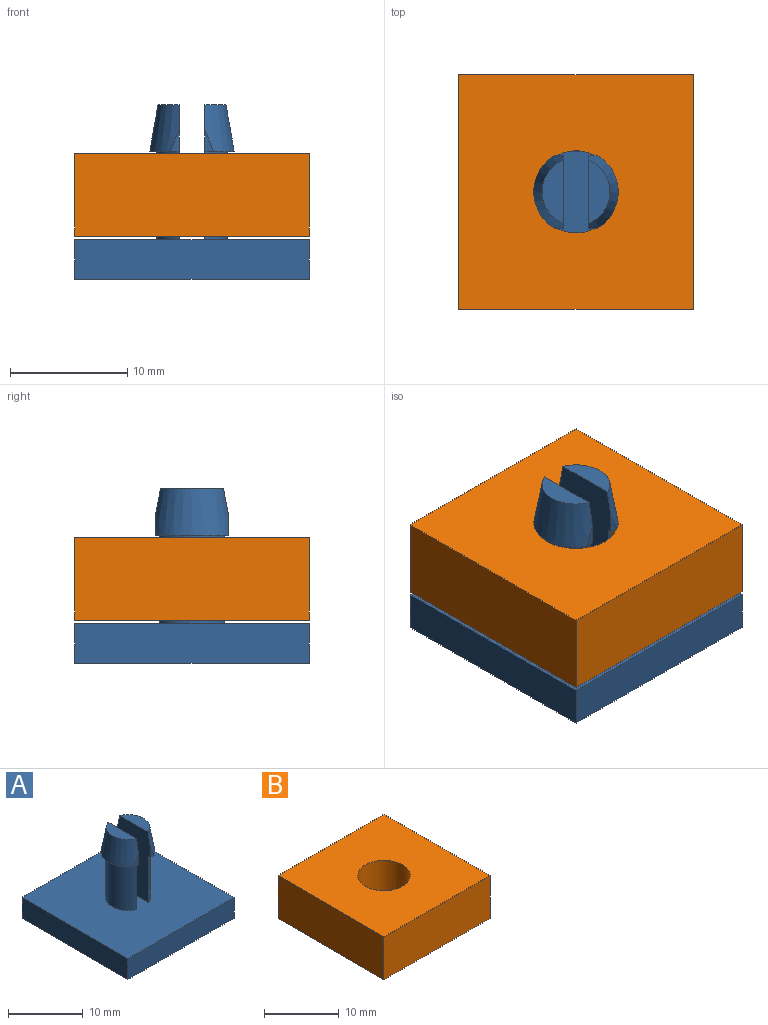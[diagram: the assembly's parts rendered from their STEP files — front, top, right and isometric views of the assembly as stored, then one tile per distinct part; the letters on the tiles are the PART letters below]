
ASSEMBLY  parts=2 mates=1
PART A: 20 faces, bbox 20.1x20.1x15 mm
  f0: plane 6.2x2.5mm, normal (0,0,-1), area 4.6mm2, adj f2,f12,f13,f16,f17
  f1: cone r=3.6mm half-angle=10deg, axis (0,0,-1), area 30.9mm2, adj f3,f11,f14,f18,f19
  f2: cone r=3.6mm half-angle=10deg, axis (0,0,-1), area 30.9mm2, adj f0,f13,f15,f16,f17
  f3: plane 5.36x1.79mm, normal (0,0,1), area 7mm2, adj f1,f11
  f4: plane 20x3.4mm, normal (0,-1,0), area 68mm2, adj f5,f7,f8,f9
  f5: plane 20x3.4mm, normal (1,0,0), area 68mm2, adj f4,f6,f8,f9
  f6: plane 20x3.4mm, normal (0,1,0), area 68mm2, adj f5,f7,f8,f9
  f7: plane 20x3.4mm, normal (-1,0,0), area 68mm2, adj f4,f6,f8,f9
  f8: plane 20x20mm, normal (0,0,1), area 384.6mm2, adj f4,f5,f6,f7,f10,f11,f12,f13
  f9: plane 20x20mm, normal (0,0,-1), area 400mm2, adj f4,f5,f6,f7
  f10: cylinder r=3mm len=7.5mm, axis (0,0,-1), area 53.8mm2, adj f8,f11,f14
  f11: plane 11.51x6.21mm, normal (1,0,0), area 65.7mm2, adj f1,f3,f8,f10,f14,f18,f19
  f12: cylinder r=3mm len=7.5mm, axis (0,0,-1), area 53.8mm2, adj f0,f8,f13
  f13: plane 11.51x6.21mm, normal (-1,0,0), area 65.7mm2, adj f0,f2,f8,f12,f15,f16,f17
  f14: plane 6.2x2.5mm, normal (0,0,-1), area 4.6mm2, adj f1,f10,f11,f18,f19
  f15: plane 5.36x1.79mm, normal (0,0,1), area 7mm2, adj f2,f13
  f16: plane 1.85x0.82mm, normal (0,1,0), area 0.7mm2, adj f0,f2,f13
  f17: plane 1.85x0.82mm, normal (0,-1,0), area 0.7mm2, adj f0,f2,f13
  f18: plane 1.85x0.82mm, normal (0,1,0), area 0.7mm2, adj f1,f11,f14
  f19: plane 1.85x0.82mm, normal (0,-1,0), area 0.7mm2, adj f1,f11,f14
PART B: 7 faces, bbox 20x20x7 mm
  f0: plane 20x7mm, normal (0,-1,0), area 140mm2, adj f1,f3,f4,f5
  f1: plane 20x7mm, normal (1,0,0), area 140mm2, adj f0,f2,f4,f5
  f2: plane 20x7mm, normal (0,1,0), area 140mm2, adj f1,f3,f4,f5
  f3: plane 20x7mm, normal (-1,0,0), area 140mm2, adj f0,f2,f4,f5
  f4: plane 20x20mm, normal (0,0,1), area 361.5mm2, adj f0,f1,f2,f3,f6
  f5: plane 20x20mm, normal (0,0,-1), area 361.5mm2, adj f0,f1,f2,f3,f6
  f6: cylinder r=3.5mm len=7mm, axis (0,0,1), area 153.9mm2, adj f4,f5
PLACE A at identity
PLACE B t=(0,0,-0.2)mm
MATE parallel B.f4 <-> A.f8  axis (0,0,1) through (-10,-10,10.7)mm
